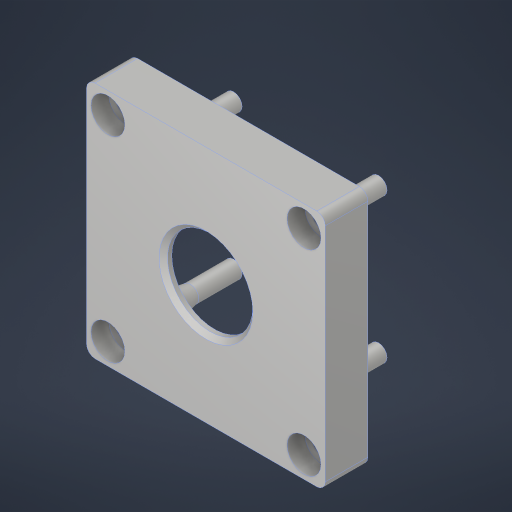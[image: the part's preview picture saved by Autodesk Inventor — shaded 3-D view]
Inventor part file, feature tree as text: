
AUTODESK INVENTOR PART (.ipt)
format: ipt  version: 2023 (Build 270158000, 158)  size: 399,360 bytes
history: native  units: in
note: dims shown in document units (in); Inventor stores cm internally (conversion verified against a paired STEP export)
features: sketch x6, hole x3, other x2, extrude x2, fillet x2, chamfer x2, shell x1, revolve x1
ambient origin geometry x8: Origin, YZ Plane, XZ Plane, XY Plane, X Axis, Y Axis, Z Axis, Center Point
bodies: Solid1 (feature_tree)
feature tree (19):
  other  "ELP Camera Case.ipt"
  sketch  "Sketch2"  dims[d10=0.0787in d11=0.0787in]
  extrude  "Extrusion1"  Depth=0.3937in TaperAngle=0.0deg
  hole  "Hole4"  [1 undecoded]
  shell  "Shell1"  Thickness=0.0394in
  fillet  "Fillet1"  Radius=0.3779in
  extrude  "Extrusion2"  TaperAngle=90.0deg  [1 undecoded]
  hole  "Hole2"  [1 undecoded]
  chamfer  "Chamfer1"  [1 undecoded]
  hole  "Hole3"  [1 undecoded]
  chamfer  "Chamfer2"  [1 undecoded]
  fillet  "Fillet2"  [1 undecoded]
  sketch  "Sketch1"  dims[d0=0.3937in d1=0.3937in d2=0.0in]
  sketch  "Sketch3"  dims[d12=0.3937in d13=0.5315in d14=0.0in d15=0.0in]
  sketch  "Sketch4"  dims[d16=0.0827in d17=0.2362in d18=0.1575in d19=0.0787in d20=90.0deg d21=0.0787in d22=0.0in]
  sketch  "Sketch5"  dims[d23=0.0787in d24=0.0787in d25=0.5497in]
  other  "Srf1"
  sketch  "Sketch6"  dims[d26=0.7874in d27=0.2362in d28=0.1575in d29=0.0787in d30=90.0deg d31=0.0787in d32=0.0in d33=0.0394in d34=0.0787in d35=0.5497in d36=0.3779in d37=90.0deg d38=0.177in d39=0.2362in d40=0.3125in d41=0.164in d42=0.5635in d43=0.315in d44=0.8108in d45=0.0394in d46=0.0in d47=0.0in d48=0.0in]
  revolve  "RevolutionSrf1"  [1 undecoded]
note: 8 required parameter values undecoded (feature->parameter linkage not recoverable at this tier; creation-order binding heuristic only, values carry confidence <= 0.55)
